FCSTD DOCUMENT
Label: EndPlate4
objects: Sketcher::SketchObject×1
note: 1 computed .brp shape members not serialized (recipe doc carries the construction recipe); baked Part::Feature solids carry a one-line shape summary decoded from their .brp

FEATURE [Sketcher::SketchObject] Sketch
  sketch-geometry (38):
    g0: LineSegment StartX=0 StartY=95 StartZ=0 EndX=0 EndY=5 EndZ=0
    g1: LineSegment StartX=5 StartY=0 StartZ=0 EndX=95 EndY=0 EndZ=0
    g2: LineSegment StartX=100 StartY=5 StartZ=0 EndX=100 EndY=95 EndZ=0
    g3: LineSegment StartX=5 StartY=100 StartZ=0 EndX=95 EndY=100 EndZ=0
    g4: LineSegment StartX=17.2018 StartY=95 StartZ=0 EndX=82.7982 EndY=95 EndZ=0
    g5: LineSegment StartX=85.6655 StartY=88.2441 StartZ=0 EndX=52.8673 EndY=54.288 EndZ=0
    g6: LineSegment StartX=47.1327 StartY=54.288 StartZ=0 EndX=14.3345 EndY=88.2441 EndZ=0
    g7: LineSegment StartX=10.1578 StartY=86.7934 StartZ=0 EndX=44.1598 EndY=51.591 EndZ=0
    g8: LineSegment StartX=5 StartY=84.7092 StartZ=0 EndX=5 EndY=14.3044 EndZ=0
    g9: LineSegment StartX=10.1578 StartY=12.2202 StartZ=0 EndX=44.1598 EndY=47.4226 EndZ=0
    g10: LineSegment StartX=47.8422 StartY=44.0402 StartZ=0 EndX=15.044 EndY=10.0842 EndZ=0
    g11: LineSegment StartX=17.2018 StartY=5 StartZ=0 EndX=82.7982 EndY=5 EndZ=0
    g12: LineSegment StartX=84.956 StartY=10.0842 StartZ=0 EndX=52.1578 EndY=44.0403 EndZ=0
    g13: LineSegment StartX=55.8402 StartY=47.4226 StartZ=0 EndX=89.8422 EndY=12.2202 EndZ=0
    g14: LineSegment StartX=95 StartY=14.3044 StartZ=0 EndX=95 EndY=84.7092 EndZ=0
    g15: LineSegment StartX=89.8422 StartY=86.7934 StartZ=0 EndX=55.8402 EndY=51.591 EndZ=0
    g16: ArcOfCircle CenterX=95 CenterY=95 CenterZ=0 NormalX=0 NormalY=0 NormalZ=1 Radius=5 StartAngle=6.28319 EndAngle=7.85398
    g17: ArcOfCircle CenterX=95 CenterY=5 CenterZ=0 NormalX=0 NormalY=0 NormalZ=1 Radius=5 StartAngle=4.71239 EndAngle=6.28318
    g18: ArcOfCircle CenterX=5 CenterY=5 CenterZ=0 NormalX=0 NormalY=0 NormalZ=1 Radius=5 StartAngle=3.14159 EndAngle=4.71239
    g19: ArcOfCircle CenterX=5 CenterY=95 CenterZ=0 NormalX=0 NormalY=0 NormalZ=1 Radius=5 StartAngle=1.5708 EndAngle=3.14159
    g20: ArcOfCircle CenterX=17.2018 CenterY=91.0136 CenterZ=0 NormalX=0 NormalY=0 NormalZ=1 Radius=3.98643 StartAngle=1.5708 EndAngle=3.90965
    g21: ArcOfCircle CenterX=82.7982 CenterY=91.0136 CenterZ=0 NormalX=0 NormalY=0 NormalZ=1 Radius=3.98643 StartAngle=5.51513 EndAngle=7.85398
    g22: ArcOfCircle CenterX=50 CenterY=57.0575 CenterZ=0 NormalX=0 NormalY=0 NormalZ=1 Radius=3.98643 StartAngle=3.90965 EndAngle=5.51513
    g23: ArcOfCircle CenterX=92 CenterY=84.7092 CenterZ=0 NormalX=0 NormalY=0 NormalZ=1 Radius=3 StartAngle=6.05302e-07 EndAngle=2.37354
    g24: ArcOfCircle CenterX=92 CenterY=14.3044 CenterZ=0 NormalX=0 NormalY=0 NormalZ=1 Radius=3 StartAngle=3.90965 EndAngle=6.28318
    g25: ArcOfCircle CenterX=57.998 CenterY=49.5068 CenterZ=0 NormalX=0 NormalY=0 NormalZ=1 Radius=3 StartAngle=2.37353 EndAngle=3.90965
    g26: ArcOfCircle CenterX=82.7982 CenterY=8 CenterZ=0 NormalX=0 NormalY=0 NormalZ=1 Radius=3 StartAngle=4.71239 EndAngle=7.05124
    g27: ArcOfCircle CenterX=17.2018 CenterY=8 CenterZ=0 NormalX=0 NormalY=0 NormalZ=1 Radius=3 StartAngle=2.37354 EndAngle=4.71239
    g28: ArcOfCircle CenterX=8 CenterY=14.3044 CenterZ=0 NormalX=0 NormalY=0 NormalZ=1 Radius=3 StartAngle=3.14159 EndAngle=5.51513
    g29: ArcOfCircle CenterX=8 CenterY=84.7092 CenterZ=0 NormalX=0 NormalY=0 NormalZ=1 Radius=3 StartAngle=0.768056 EndAngle=3.14159
    g30: ArcOfCircle CenterX=42.002 CenterY=49.5068 CenterZ=0 NormalX=0 NormalY=0 NormalZ=1 Radius=3 StartAngle=5.51513 EndAngle=7.05124
    g31: LineSegment [constr] StartX=50 StartY=57.0575 StartZ=0 EndX=50 EndY=49.5068 EndZ=0
    g32: LineSegment [constr] StartX=50 StartY=49.5068 StartZ=0 EndX=50 EndY=41.956 EndZ=0
    g33: ArcOfCircle CenterX=50 CenterY=41.956 CenterZ=0 NormalX=0 NormalY=0 NormalZ=1 Radius=3 StartAngle=0.768062 EndAngle=2.37354
    g34: LineSegment [constr] StartX=42.002 StartY=49.5068 StartZ=0 EndX=50 EndY=49.5068 EndZ=0
    g35: LineSegment [constr] StartX=50 StartY=49.5068 StartZ=0 EndX=57.998 EndY=49.5068 EndZ=0
    g36: LineSegment [constr] StartX=52.1578 StartY=44.0403 StartZ=0 EndX=55.8402 EndY=47.4226 EndZ=0
    g37: LineSegment [constr] StartX=44.1598 StartY=47.4226 StartZ=0 EndX=47.8422 EndY=44.0402 EndZ=0
  constraints (124):
    c: Vertical(g0)
    c: Horizontal(g1)
    c: Vertical(g2)
    c: Horizontal(g3)
    c: Horizontal(g4)
    c: Vertical(g8)
    c: Horizontal(g11)
    c: Vertical(g14)
    c: Coincident(g3,g19)
    c: Coincident(g0,g19)
    c: Coincident(g0,g18)
    c: Coincident(g1,g18)
    c: Coincident(g1,g17)
    c: Coincident(g17,g2)
    c: Coincident(g3,g16)
    c: Coincident(g2,g16)
    c: Coincident(g4,g21)
    c: Coincident(g21,g5)
    c: Coincident(g22,g5)
    c: Coincident(g22,g6)
    c: Coincident(g6,g20)
    c: Coincident(g20,g4)
    c: Coincident(g7,g29)
    c: Coincident(g8,g29)
    c: Coincident(g30,g9)
    c: Coincident(g30,g7)
    c: Coincident(g28,g9)
    c: Coincident(g28,g8)
    c: Coincident(g10,g27)
    c: Coincident(g27,g11)
    c: Coincident(g12,g26)
    c: Coincident(g26,g11)
    c: Coincident(g24,g13)
    c: Coincident(g14,g24)
    c: Coincident(g13,g25)
    c: Coincident(g25,g15)
    c: Coincident(g15,g23)
    c: Coincident(g14,g23)
    c: DistanceY(g1) = 0
    c: DistanceX(g0) = 0
    c: Tangent(g19,g3)
    c: Tangent(g0,g19)
    c: Tangent(g18,g0)
    c: Tangent(g18,g1)
    c: Tangent(g17,g1)
    c: Tangent(g17,g2)
    c: Tangent(g2,g16)
    c: Tangent(g16,g3)
    c: Tangent(g6,g20)
    c: Tangent(g4,g20)
    c: Tangent(g4,g21)
    c: Tangent(g21,g5)
    c: Tangent(g5,g22)
    c: Tangent(g22,g6)
    c: Tangent(g15,g23)
    c: Tangent(g23,g14)
    c: Tangent(g24,g14)
    c: Tangent(g24,g13)
    c: Tangent(g13,g25)
    c: Tangent(g25,g15)
    c: Tangent(g12,g26)
    c: Tangent(g26,g11)
    c: Tangent(g11,g27)
    c: Tangent(g27,g10)
    c: Tangent(g9,g30)
    c: Tangent(g30,g7)
    c: Tangent(g7,g29)
    c: Tangent(g29,g8)
    c: Tangent(g8,g28)
    c: Tangent(g28,g9)
    c: Radius(g18) = 5
    c: Equal(g18,g19)
    c: Equal(g19,g16)
    c: Equal(g16,g17)
    c: DistanceX(g8,g0) = -5
    c: DistanceY(g4,g3) = 5
    c: DistanceY(g11,g1) = -5
    c: DistanceX(g14,g2) = 5
    c: Radius(g29) = 3
    c: Equal(g29,g28)
    c: Equal(g28,g30)
    c: Equal(g29,g25)
    c: Equal(g25,g23)
    c: Equal(g23,g24)
    c: Equal(g20,g21)
    c: Equal(g21,g22)
    c: Equal(g27,g26)
    c: Equal(g26,g29)
    c: Parallel(g7,g6)
    c: Parallel(g6,g13)
    c: Parallel(g13,g12)
    c: Parallel(g9,g10)
    c: Parallel(g10,g5)
    c: Parallel(g5,g15)
    c: Equal(g13,g9)
    c: Equal(g14,g8)
    c: Equal(g11,g4)
    c: DistanceY(g3,g1) = -100
    c: DistanceX(g2,g0) = -100
    c: Vertical(g31)
    c: Coincident(g31,g32)
    c: Vertical(g32)
    c: Equal(g32,g31)
    c: Coincident(g31,g22)
    c: Coincident(g12,g33)
    c: Coincident(g32,g33)
    c: Coincident(g33,g10)
    c: Tangent(g10,g33)
    c: Tangent(g33,g12)
    c: Equal(g29,g33)
    c: Horizontal(g34)
    c: Coincident(g31,g34)
    c: Coincident(g34,g30)
    c: Horizontal(g35)
    c: Coincident(g35,g25)
    c: Coincident(g35,g31)
    c: Equal(g35,g34)
    c: Tangent(g36,g23)
    c: Coincident(g13,g36)
    c: Coincident(g36,g12)
    c: Distance(g36) = 5
    c: Coincident(g10,g37)
    c: Coincident(g37,g9)
    c: Distance(g37) = 5
